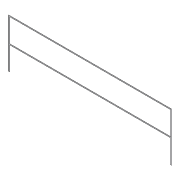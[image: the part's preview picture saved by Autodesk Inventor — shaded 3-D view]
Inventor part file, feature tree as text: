
AUTODESK INVENTOR PART (.ipt)
format: ipt  version: 2012 (Build 160160000, 160)  size: 83,456 bytes
history: native  units: in
note: dims shown in document units (in); Inventor stores cm internally (conversion verified against a paired STEP export)
features: extrude x2, sketch x1
ambient origin geometry x8: Origin, YZ Plane, XZ Plane, XY Plane, X Axis, Y Axis, Z Axis, Center Point
bodies: Solid1 (feature_tree)
feature tree (3):
  sketch  "Sketch1"  dims[d0=2.0in d1=2.0in d4=96.0in d7=0.25in d8=0.0in d11=0.25in d12=0.0in d14=48.0in d15=320.75in d16=2.0in]
  extrude  "Extrusion1"  Depth=2.0in
  extrude  "Extrusion3"  Depth=96.0in
